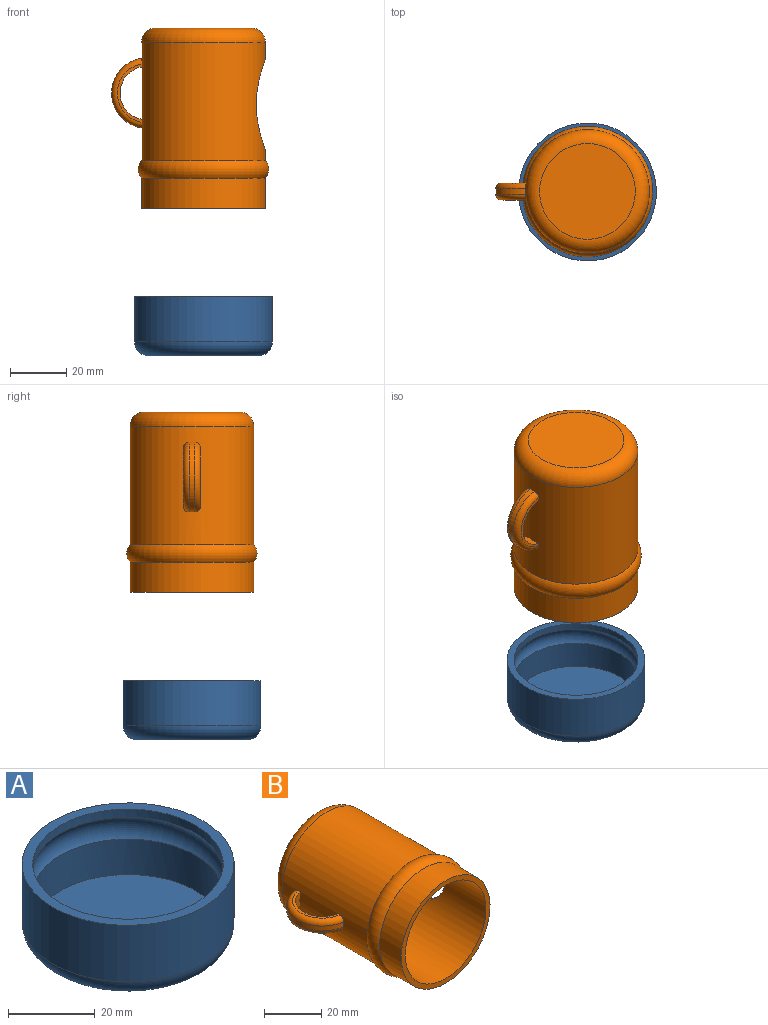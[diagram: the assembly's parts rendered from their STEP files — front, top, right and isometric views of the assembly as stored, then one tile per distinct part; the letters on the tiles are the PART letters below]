
ASSEMBLY  parts=2 mates=1
PART A: 8 faces, bbox 53x53x21 mm
  f0: cylinder r=22mm len=44mm, axis (0,0,-1), area 316mm2, adj f2,f4
  f1: cylinder r=24.5mm len=49mm, axis (0,0,-1), area 2463mm2, adj f2,f7
  f2: plane 49x49mm, normal (0,0,1), area 365.2mm2, adj f0,f1
  f3: plane 39x39mm, normal (0,0,-1), area 1194.6mm2, adj f7
  f4: torus R=18.75mm, axis (0,0,-1), area 979.2mm2, adj f0,f6
  f5: plane 44x44mm, normal (0,0,1), area 1520.5mm2, adj f6
  f6: cylinder r=22mm len=44mm, axis (0,0,-1), area 1385.6mm2, adj f4,f5
  f7: torus R=19.5mm, axis (0,0,1), area 1119.4mm2, adj f1,f3
PART B: 19 faces, bbox 58.8x64x50.2 mm
  f0: cylinder r=20mm len=62mm, axis (0,-1,0), area 7166.8mm2, adj f4,f5,f7,f8,f9,f10,f18
  f1: cylinder r=22mm len=44mm, axis (0,-1,0), area 5179mm2, adj f2,f11,f12,f13,f14,f15,f16,f17
  f2: torus R=18.49mm, axis (0,-1,0), area 968.2mm2, adj f1,f3
  f3: cylinder r=22mm len=44mm, axis (0,-1,0), area 1479.6mm2, adj f2,f4
  f4: plane 44x44mm, normal (0,-1,0), area 263.9mm2, adj f0,f3
  f5: plane 40x40mm, normal (0,-1,0), area 1256.6mm2, adj f0
  f6: plane 34x34mm, normal (0,1,0), area 907.9mm2, adj f15
  f7: plane 3x2.62mm, normal (1,0.01,0), area 5.2mm2, adj f0,f8
  f8: cylinder r=12.51mm len=2.62mm, axis (0,0,-1), area 0.1mm2, adj f0,f7
  f9: cylinder r=12.51mm len=2.62mm, axis (0,0,-1), area 0.1mm2, adj f0,f10
  f10: plane 3x2.62mm, normal (1,-0.01,0), area 5.2mm2, adj f0,f9
  f11: plane 20.76x8.85mm, normal (0,0,1), area 28.1mm2, adj f1,f14,f17
  f12: plane 20.76x8.85mm, normal (0,0,-1), area 28.1mm2, adj f1,f14,f16
  f13: cylinder r=12.51mm len=24.75mm, axis (0,0,-1), area 71.1mm2, adj f1,f16,f17
  f14: cylinder r=9.51mm len=18.73mm, axis (0,0,-1), area 157.6mm2, adj f1,f11,f12
  f15: torus R=17mm, axis (0,-1,0), area 996mm2, adj f1,f6
  f16: torus R=10.51mm, axis (0,0,1), area 105.3mm2, adj f1,f12,f13
  f17: torus R=10.51mm, axis (0,0,1), area 105.3mm2, adj f1,f11,f13
  f18: extruded ~32.43x23mm, area 193.1mm2, adj f0,f1
PLACE A rot(axis=(0,0,-1),90deg) t=(0,0,-50)mm
PLACE B rot(axis=(1,0,0),90deg) t=(0,0,10.74)mm fixed
MATE slider B.f0 <-> A.f0  axis (0,0,-1) through (0,0,-8)mm
